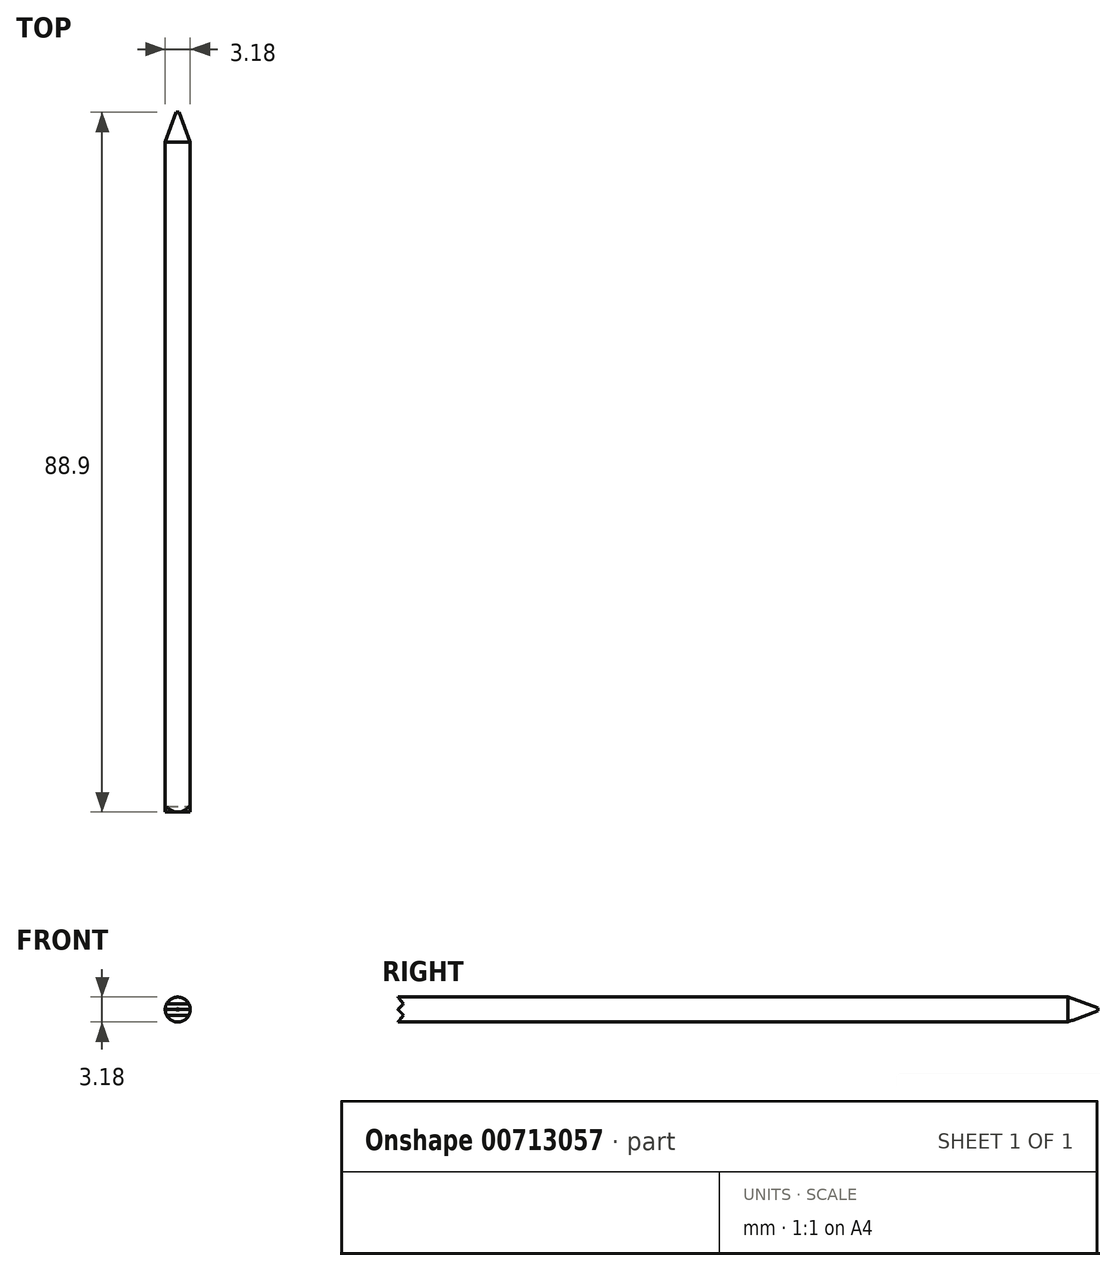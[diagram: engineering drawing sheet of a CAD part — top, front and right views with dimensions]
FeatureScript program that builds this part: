
annotation { "Feature Type Name" : "Feature", "Feature Type Description" : "" }
export const myFeature = defineFeature(function(context is Context, id is Id, definition is map)
    precondition{}
    {
        {
            var Q0;
            Q0=qCreatedBy(makeId("Front.planeOp"),FACE);
            var sketch = newSketch(context, id + "F0", { "sketchPlane" : qUnion([Q0])});
            skCircle(sketch, "E0", {"center": v(0, 0) * mm, "radius": 1.59 * mm});
            skSolve(sketch);
        }
        {
            var Q0;
            Q0 = qSketchRegion(id + "F0", true);
            extrude(context, id + "F1", {"entities" : qUnion([Q0]), "oppositeDirection" : true, "depth" : 88.9 * mm, "offsetDistance" : 25.4 * mm});
        }
        {
            var Q0;
            Q0=makeQuery(id+"F1.opExtrude","CAP_EDGE",EDGE,{"disambiguationData":[OSD([sQuery(id+"F0.wireOp",EDGE,"E0")])],"isStart":false});
            chamfer(context, id + "F2", {"entities" : qUnion([Q0]), "chamferType" : ChamferType.OFFSET_ANGLE, "width" : 3.8 * mm, "oppositeDirection" : false, "angle" : 20 * degree, "tangentPropagation" : true});
        }
        {
            var Q0;
            Q0=qCreatedBy(makeId("Right.planeOp"),FACE);
            var sketch = newSketch(context, id + "F3", { "sketchPlane" : qUnion([Q0])});
            skLineSegment(sketch, "E1", {"start": v(0, 1.59) * mm, "end": v(85.1, 1.59) * mm});
            skLineSegment(sketch, "E2", {"start": v(85.1, -1.59) * mm, "end": v(0, -1.59) * mm});
            skLineSegment(sketch, "E3", {"start": v(0, 1.59) * mm, "end": v(0.7, 0.7) * mm});
            skLineSegment(sketch, "E4", {"start": v(0.7, 0.7) * mm, "end": v(0, 0) * mm});
            skLineSegment(sketch, "E5", {"start": v(0, 0) * mm, "end": v(0.7, -0.7) * mm});
            skLineSegment(sketch, "E6", {"start": v(0.7, -0.7) * mm, "end": v(0, -1.59) * mm});
            skLineSegment(sketch, "E7", {"start": v(0, 1.59) * mm, "end": v(0, -1.59) * mm});
            skSolve(sketch);
        }
        {
            var Q0;
            Q0 = qSketchRegion(id + "F3", true);
            extrude(context, id + "F4", {"entities" : qUnion([Q0]), "operationType" : NewBodyOperationType.REMOVE, "oppositeDirection" : true, "depth" : 25.4 * mm, "offsetDistance" : 25.4 * mm});
        }
        {
            var Q0;
            Q0 = qSketchRegion(id + "F3", true);
            extrude(context, id + "F5", {"entities" : qUnion([Q0]), "operationType" : NewBodyOperationType.REMOVE, "depth" : 25.4 * mm, "offsetDistance" : 25.4 * mm});
        }
    });
